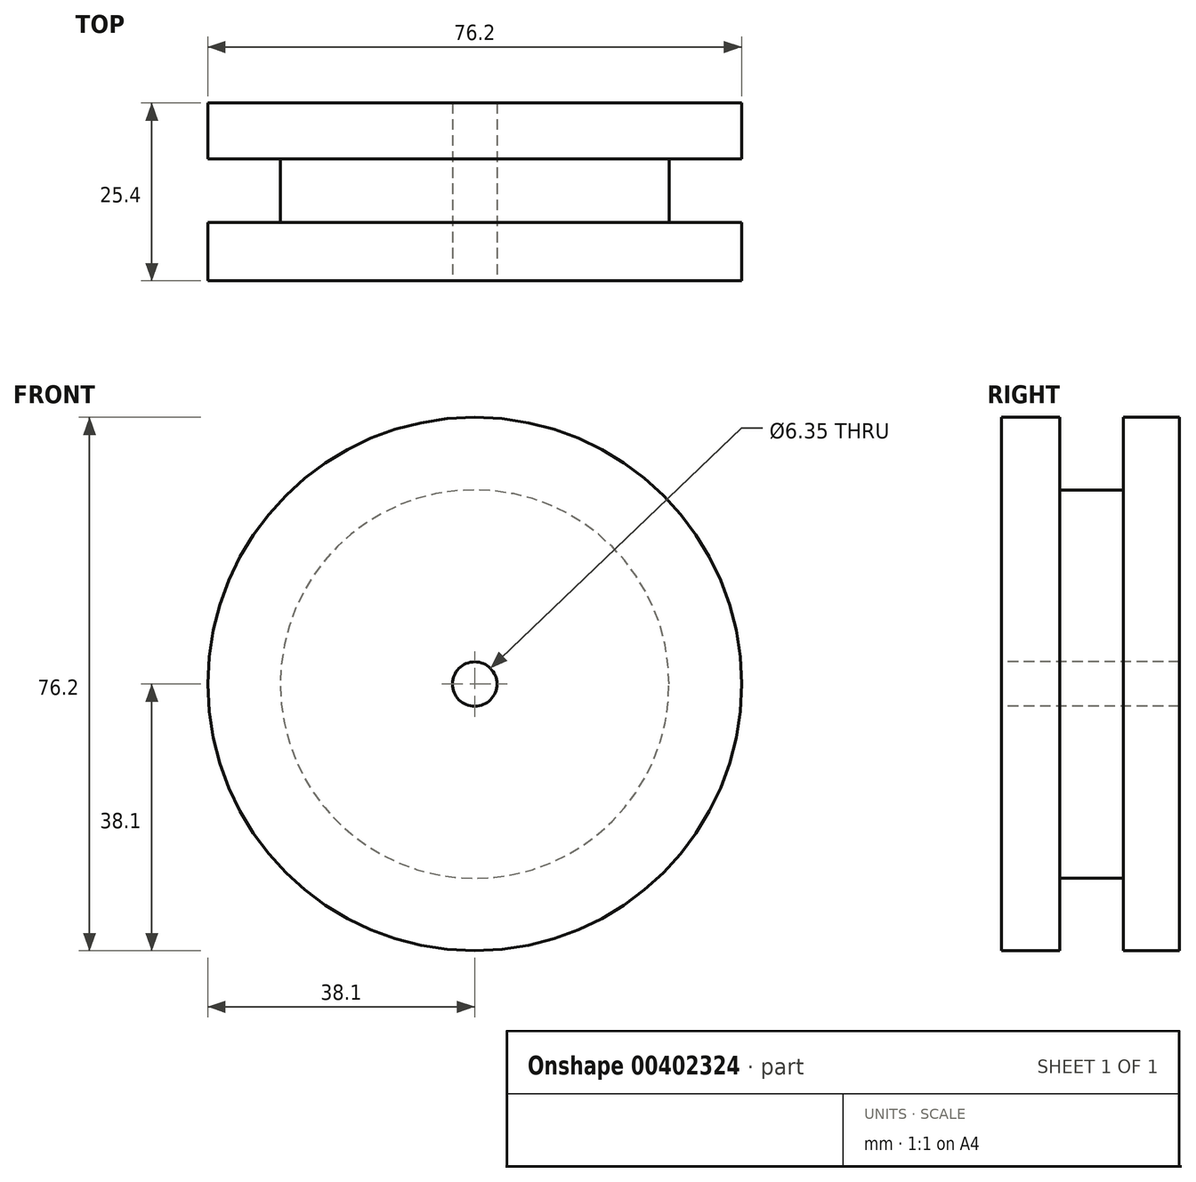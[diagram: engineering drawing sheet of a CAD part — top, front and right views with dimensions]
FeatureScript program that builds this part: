
annotation { "Feature Type Name" : "Feature", "Feature Type Description" : "" }
export const myFeature = defineFeature(function(context is Context, id is Id, definition is map)
    precondition{}
    {
        {
            var Q0;
            Q0=qCreatedBy(makeId("Front.planeOp"),FACE);
            var sketch = newSketch(context, id + "F0", { "sketchPlane" : qUnion([Q0])});
            skCircle(sketch, "E0", {"center": v(0, 0) * mm, "radius": 38.1 * mm});
            skSolve(sketch);
        }
        {
            var Q0;
            Q0 = qSketchRegion(id + "F0", true);
            extrude(context, id + "F1", {"entities" : qUnion([Q0]), "depth" : 25.4 * mm, "symmetric" : true});
        }
        {
            var Q0;
            Q0=qCreatedBy(makeId("Top.planeOp"),FACE);
            var sketch = newSketch(context, id + "F2", { "sketchPlane" : qUnion([Q0])});
            skLineSegment(sketch, "E1.bottom", {"start": v(-27.74, 4.72) * mm, "end": v(-47.77, 4.72) * mm});
            skLineSegment(sketch, "E1.top", {"start": v(-27.74, -4.36) * mm, "end": v(-47.77, -4.36) * mm});
            skLineSegment(sketch, "E1.left", {"start": v(-27.74, 4.72) * mm, "end": v(-27.74, -4.36) * mm});
            skLineSegment(sketch, "E1.right", {"start": v(-47.77, 4.72) * mm, "end": v(-47.77, -4.36) * mm});
            skLineSegment(sketch, "E2", {"start": v(0, 7.62) * mm, "end": v(0, -8.35) * mm});
            skSolve(sketch);
        }
        {
            var Q0;
            Q0=makeQuery(id+"F2.imprint","IMPRINT",FACE,{"disambiguationData":[TD([[makeQuery(id+"F2.imprint","IMPRINT",EDGE,{"derivedFrom":sQuery(id+"F2.wireOp",EDGE,"E1.bottom")}),1.0]])]});
            var Q1;
            Q1=sQuery(id+"F2.wireOp",EDGE,"E2");
            revolve(context, id + "F3", {"operationType" : NewBodyOperationType.REMOVE, "entities" : qUnion([Q0]), "axis" : qUnion([Q1]), "revolveType" : RevolveType.FULL, "oppositeDirection" : true});
        }
        {
            var Q0;
            Q0=makeQuery(id+"F1.opExtrude","CAP_FACE",FACE,{"disambiguationData":[OSD([sQuery(id+"F0.wireOp",EDGE,"E0")])],"isStart":false});
            var sketch = newSketch(context, id + "F4", { "sketchPlane" : qUnion([Q0])});
            skCircle(sketch, "E3", {"center": v(0, 0) * mm, "radius": 3.18 * mm});
            skSolve(sketch);
        }
        {
            var Q0;
            Q0 = qSketchRegion(id + "F4", true);
            extrude(context, id + "F5", {"entities" : qUnion([Q0]), "operationType" : NewBodyOperationType.REMOVE, "endBound" : BoundingType.THROUGH_ALL, "oppositeDirection" : true, "depth" : 25.4 * mm});
        }
    });
